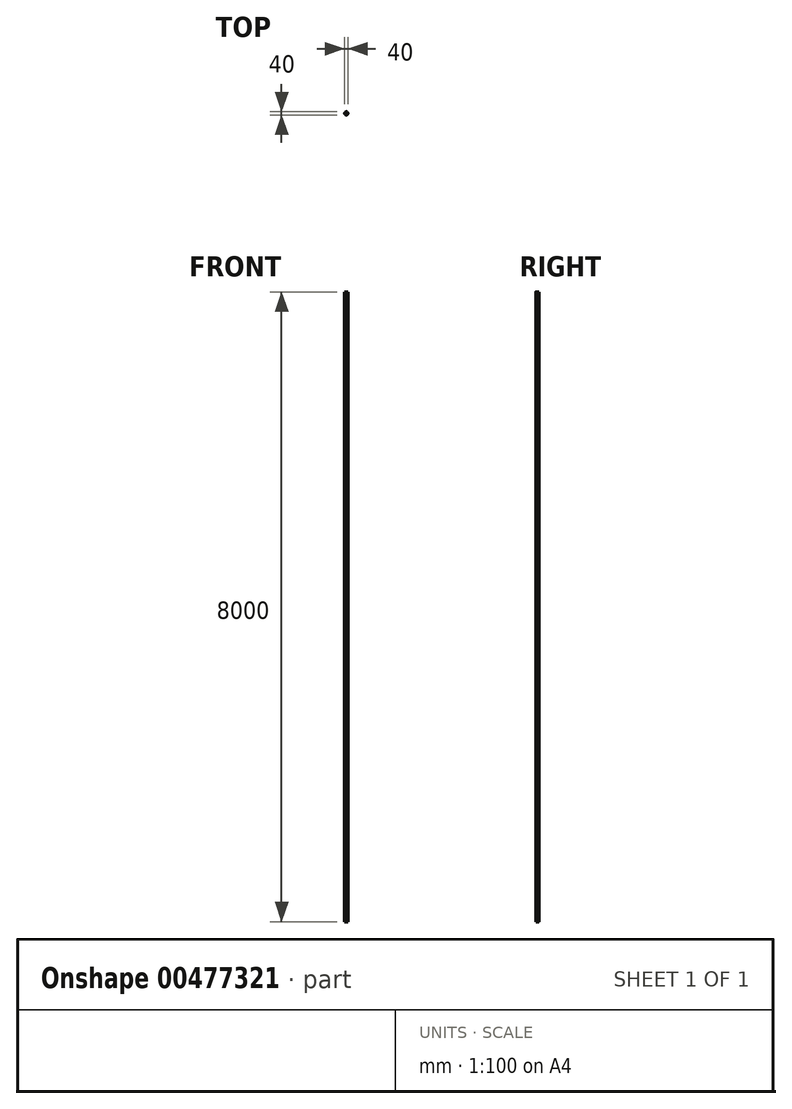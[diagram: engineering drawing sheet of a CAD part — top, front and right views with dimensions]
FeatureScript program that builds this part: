
annotation { "Feature Type Name" : "Feature", "Feature Type Description" : "" }
export const myFeature = defineFeature(function(context is Context, id is Id, definition is map)
    precondition{}
    {
        {
            var Q0;
            Q0=qCreatedBy(makeId("Top.planeOp"),FACE);
            var sketch = newSketch(context, id + "F0", { "sketchPlane" : qUnion([Q0])});
            skCircle(sketch, "E0", {"center": v(0, 0) * mm, "radius": 20 * mm});
            skSolve(sketch);
        }
        {
            var Q0;
            Q0=makeQuery(id+"F0.imprint","IMPRINT",FACE,{"disambiguationData":[TD([[makeQuery(id+"F0.imprint","IMPRINT",EDGE,{"derivedFrom":sQuery(id+"F0.wireOp",EDGE,"E0")}),1.0]])]});
            extrude(context, id + "F1", {"entities" : qUnion([Q0]), "depth" : 8000 * mm});
        }
    });
